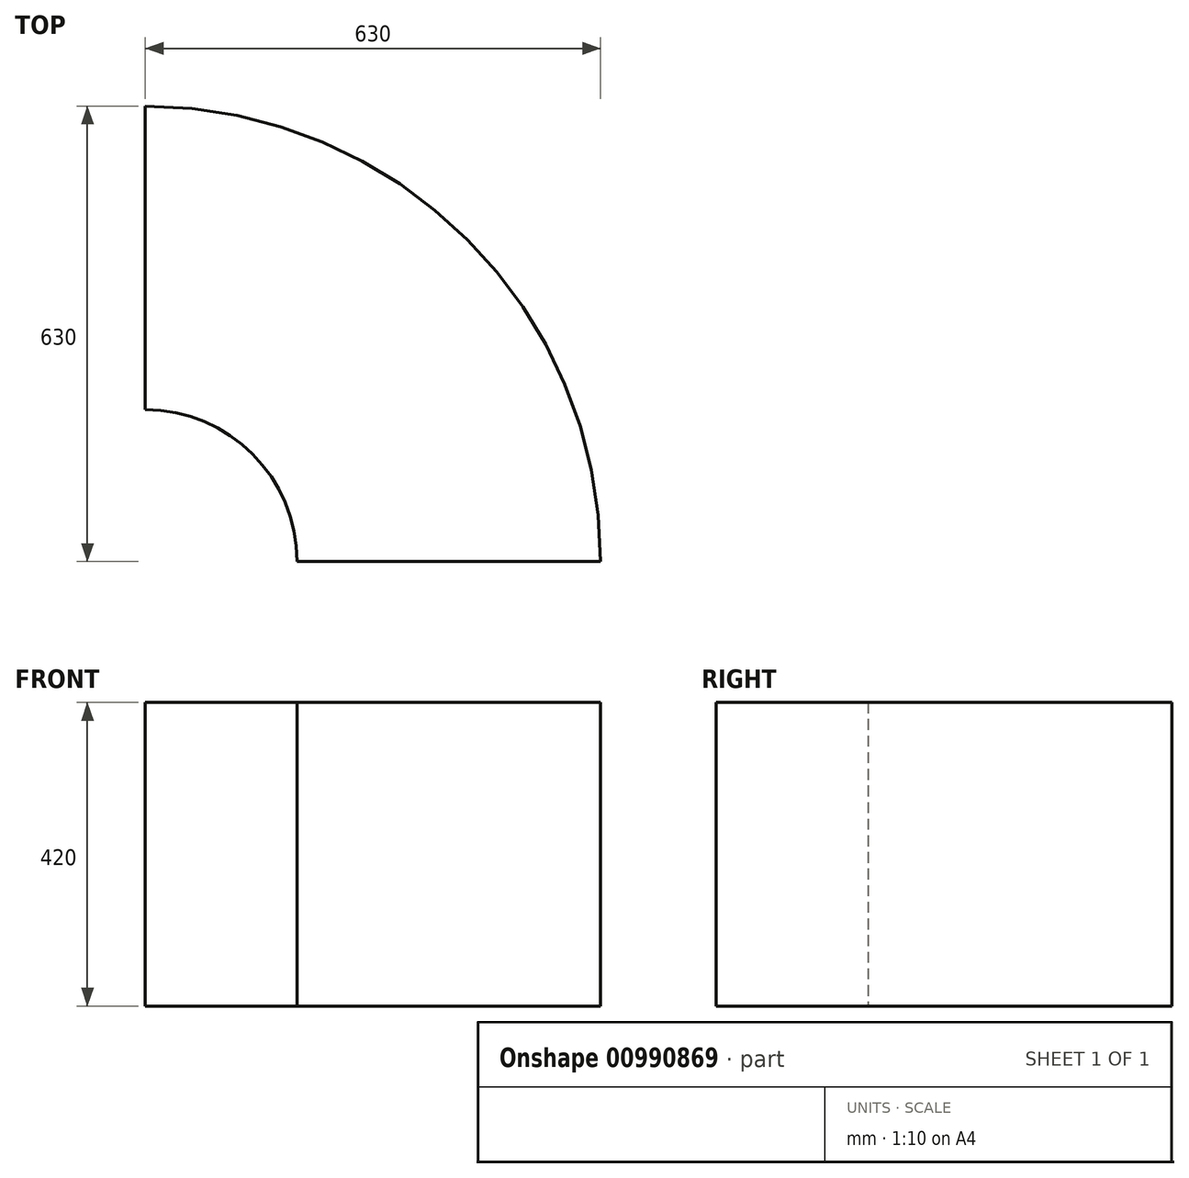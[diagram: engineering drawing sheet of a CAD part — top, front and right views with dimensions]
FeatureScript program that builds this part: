
annotation { "Feature Type Name" : "Feature", "Feature Type Description" : "" }
export const myFeature = defineFeature(function(context is Context, id is Id, definition is map)
    precondition{}
    {
        {
            var Q0;
            Q0=qCreatedBy(makeId("Top.planeOp"),FACE);
            var sketch = newSketch(context, id + "F0", { "sketchPlane" : qUnion([Q0])});
            skArc(sketch, "E0", {"start": v(-1675.87, -73.89) * mm, "mid": v(-1737.37, 74.6) * mm, "end": v(-1885.87, 136.11) * mm});
            skArc(sketch, "E1", {"start": v(-1255.87, -73.89) * mm, "mid": v(-1440.39, 371.6) * mm, "end": v(-1885.87, 556.11) * mm});
            skLineSegment(sketch, "E2", {"start": v(-1675.87, -73.89) * mm, "end": v(-1255.87, -73.89) * mm});
            skLineSegment(sketch, "E3", {"start": v(-1885.87, 136.11) * mm, "end": v(-1885.87, 556.11) * mm});
            skSolve(sketch);
        }
        {
            var Q0;
            Q0 = qSketchRegion(id + "F0", true);
            extrude(context, id + "F1", {"entities" : qUnion([Q0]), "depth" : 420 * mm, "offsetDistance" : 25 * mm});
        }
    });
